# Revit family: Grohe_PlumbingFixtures_WallHungWCFrame_RapidSLX-39596000xxx
name_source: partatom
category: Plumbing Fixtures
revit_build: Autodesk Revit 2018 (Build: 20190510_1515(x64)
units: mm (PartAtom-declared; Revit-internal decimal feet)

## family parameters
Always vertical = Yes
Cut with Voids When Loaded = No
Part Type = Normal
Room Calculation Point = No
Round Connector Dimension = Use Diameter
Shared = No
Work Plane-Based = No

## types (1)
- Grohe_PlumbingFixtures_WallHungWCFrame_RapidSLX-39596000xxx
    ApparentLoad = 0 VA
    Assembly Code = D2010900
    AssetType = Fixed
    BIMObjectName = Grohe_PlumbingFixtures_WallHungWCFrame_RapidSLX-39596000
    CW Connection = Yes
    CisternMaterial = Grohe - ABS Plastic - White
    ClassificationName = Uniclass2015
    ClassificationValue = Pr_40_20_93_89
    Color = Blue
    Depth = 130 mm
    Description = Rapid SLX Element for WC, 1.13 m installation height with integrated socket and shower toilet connection with flushing cistern. GD 2 with integrated power socket; ready for shower toilets (water); small revision shaft for small flush plates; for on-the-wall installations or studded walls; powder-coated steel frame, self-supporting for dry-cladding; completely pre-assembled; with fixed connections; quick adjustment, lockable fixing material; TÜV approved; 2 WC fixing bolts; fixing device for ceramic; distance of fixing bolts 180/230mm; outlet bend Ø 90mm; depth adjustable; reducer Ø 90/110mm; inlet and outlet connecting set; flushing cistern GD 2, 3 - 6 l, containing following features: adjustment ex-factory 6 l and 3 l; pneumatic discharge valve offering 3 modes of operation: dual flush, start/stop or single flush; water supply from right, back or top; low noise (group I acc. to German Noise Specification); fully insulated against condensation; ½“ water supply connection including integrated angle valve and push fit flexible hose union; no tools required for the installation of the inspection shaft including protection during construction phase; for vertical use; including flow manager; reduces flow of the flush, prevents overspill in rimless toilets, easy flow regulation via inspection shaft without removing the valves; for on-the-wall installation please order wall brackets 38 558 00M (sold separately); for mounting of flush plates 156 x 197mm please order revision shaft 66 791 000 (sold separately).
    DocumentationCertificates = https://www.grohe.co.uk
    DocumentationInstallationGuide = https://www.bimstore.co
    DocumentationLiterature = https://www.bimstore.co
    DocumentationMaintenance = https://www.grohe.co.uk
    DocumentationTechnical = https://www.grohe.co.uk
    DurationUnit = Year
    ExpectedLife = 0
    Finish = Powder-coated steel
    FrameMaterial = Grohe - Powder Coated Steel - Blue
    HW Connection = No
    Height = 1085 mm
    IfcExportAs = IfcFlowTerminalType
    IfcExportType = IfcSanitaryTerminalTypeEnum.CISTERN
    Keynote = N13
    Length = 500 mm
    Manufacturer = Grohe
    ManufacturerName = Grohe
    Material = Powder-coated steel
    Model = 39596000
    ModelNumber = Rapid SLX WC 3-6 l 1,13m, Standard
    ModelReference = 39596000
    NBSDescription = Grohe - WC cisterns
    NBSObjectName = WC cisterns
    NBSReference = 45-35-70/383
    NominalDepth = 130 mm
    NominalHeight = 1085 mm
    NominalLength = 500 mm
    PlateMaterial = Grohe - Steel
    ProductionYear = 2020
    Size = 500mm(l) x 130mm(d)
    Type Comments = Rapid SLX WC 3-6 l 1,13m, Standard
    TypeName = 39596000
    URL = https://www.grohe.co.uk
    Vent Connection = No
    Voltage = 0 V
    WarrantyDurationLabor = 0
    WarrantyDurationParts = 0
    WarrantyDurationUnit = Year
    Waste Connection = Yes
    _BSBibleVersion = 16
    _BimSpecGuid = 0
    _CurrentRevision = 1
    _DistributedBy = www.bimstore.co

## geometry (parser evidence)
native form markers: Sweep x2
no freeform markers — native parametric forms only
